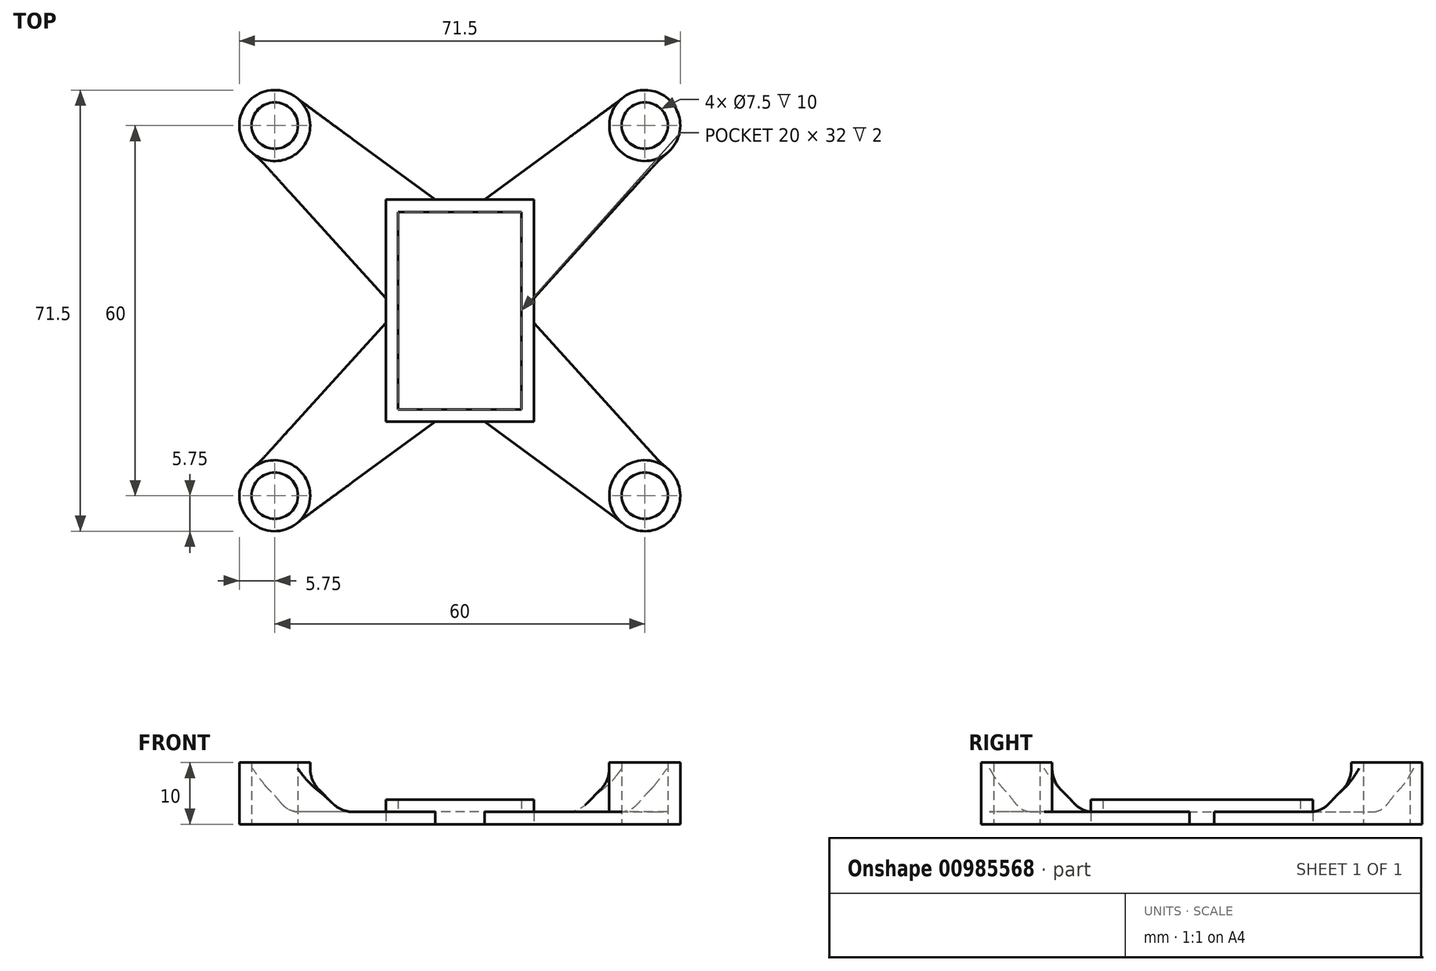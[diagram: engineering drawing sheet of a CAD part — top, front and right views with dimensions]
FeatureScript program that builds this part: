
annotation { "Feature Type Name" : "Feature", "Feature Type Description" : "" }
export const myFeature = defineFeature(function(context is Context, id is Id, definition is map)
    precondition{}
    {
        {
            var Q0;
            Q0=qCreatedBy(makeId("Top.planeOp"),FACE);
            var sketch = newSketch(context, id + "F0", { "sketchPlane" : qUnion([Q0])});
            skLineSegment(sketch, "E0.bottom", {"start": v(-30, 30) * mm, "end": v(30, 30) * mm, "construction": true});
            skLineSegment(sketch, "E0.top", {"start": v(-30, -30) * mm, "end": v(30, -30) * mm, "construction": true});
            skLineSegment(sketch, "E0.left", {"start": v(-30, 30) * mm, "end": v(-30, -30) * mm, "construction": true});
            skLineSegment(sketch, "E0.right", {"start": v(30, 30) * mm, "end": v(30, -30) * mm, "construction": true});
            skPoint(sketch, "E0.middle", {"position": v(0, 0) * mm});
            skCircle(sketch, "E1", {"center": v(-30, 30) * mm, "radius": 3.75 * mm});
            skCircle(sketch, "E2", {"center": v(30, 30) * mm, "radius": 3.75 * mm});
            skCircle(sketch, "E3", {"center": v(30, -30) * mm, "radius": 3.75 * mm});
            skCircle(sketch, "E4", {"center": v(-30, -30) * mm, "radius": 3.75 * mm});
            skCircle(sketch, "E5", {"center": v(-30, 30) * mm, "radius": 5.75 * mm});
            skCircle(sketch, "E6", {"center": v(30, 30) * mm, "radius": 5.75 * mm});
            skCircle(sketch, "E7", {"center": v(30, -30) * mm, "radius": 5.75 * mm});
            skCircle(sketch, "E8", {"center": v(-30, -30) * mm, "radius": 5.75 * mm});
            skLineSegment(sketch, "E9.bottom", {"start": v(-10, 16) * mm, "end": v(10, 16) * mm});
            skLineSegment(sketch, "E9.top", {"start": v(-10, -16) * mm, "end": v(10, -16) * mm});
            skLineSegment(sketch, "E9.left", {"start": v(-10, 16) * mm, "end": v(-10, -16) * mm});
            skLineSegment(sketch, "E9.right", {"start": v(10, 16) * mm, "end": v(10, -16) * mm});
            skLineSegment(sketch, "E10.bottom", {"start": v(-12, 18) * mm, "end": v(12, 18) * mm});
            skLineSegment(sketch, "E10.top", {"start": v(-12, -18) * mm, "end": v(12, -18) * mm});
            skLineSegment(sketch, "E10.left", {"start": v(-12, 18) * mm, "end": v(-12, -18) * mm});
            skLineSegment(sketch, "E10.right", {"start": v(12, 18) * mm, "end": v(12, -18) * mm});
            skLineSegment(sketch, "E11", {"start": v(-4, 18) * mm, "end": v(-26, 34.13) * mm});
            skLineSegment(sketch, "E12.MirrorCS", {"start": v(-12, 2) * mm, "end": v(-32.84, 25) * mm});
            skLineSegment(sketch, "E13.MirrorCS", {"start": v(4, 18) * mm, "end": v(26, 34.13) * mm});
            skLineSegment(sketch, "E14.MirrorCS", {"start": v(12, 2) * mm, "end": v(32.84, 25) * mm});
            skLineSegment(sketch, "E15.MirrorCS", {"start": v(-12, -2) * mm, "end": v(-32.84, -25) * mm});
            skLineSegment(sketch, "E16.MirrorCS", {"start": v(-4, -18) * mm, "end": v(-26, -34.13) * mm});
            skLineSegment(sketch, "E17.MirrorCS", {"start": v(4, -18) * mm, "end": v(26, -34.13) * mm});
            skLineSegment(sketch, "E18.MirrorCS", {"start": v(12, -2) * mm, "end": v(32.84, -25) * mm});
            skSolve(sketch);
        }
        {
            var Q0;
            {var subQ0=sQuery(id+"F0.wireOp",EDGE,"E11");Q0=makeQuery(id+"F0.imprint","IMPRINT",FACE,{"disambiguationData":[TD([[makeQuery(id+"F0.imprint","IMPRINT",EDGE,{"derivedFrom":subQ0}),1.0]])]});}
            var Q1;
            Q1=makeQuery(id+"F0.imprint","IMPRINT",FACE,{"disambiguationData":[TD([[makeQuery(id+"F0.imprint","IMPRINT",EDGE,{"derivedFrom":sQuery(id+"F0.wireOp",EDGE,"E1")}),-1.0]])]});
            var Q2;
            Q2=makeQuery(id+"F0.imprint","IMPRINT",FACE,{"disambiguationData":[TD([[makeQuery(id+"F0.imprint","IMPRINT",EDGE,{"derivedFrom":sQuery(id+"F0.wireOp",EDGE,"E2")}),-1.0]])]});
            var Q3;
            {var subQ0=sQuery(id+"F0.wireOp",EDGE,"E13.MirrorCS");Q3=makeQuery(id+"F0.imprint","IMPRINT",FACE,{"disambiguationData":[TD([[makeQuery(id+"F0.imprint","IMPRINT",EDGE,{"derivedFrom":subQ0}),-1.0]])]});}
            var Q4;
            Q4=makeQuery(id+"F0.imprint","IMPRINT",FACE,{"disambiguationData":[TD([[makeQuery(id+"F0.imprint","IMPRINT",EDGE,{"derivedFrom":sQuery(id+"F0.wireOp",EDGE,"E9.bottom")}),-1.0]])]});
            var Q5;
            Q5=makeQuery(id+"F0.imprint","IMPRINT",FACE,{"disambiguationData":[TD([[makeQuery(id+"F0.imprint","IMPRINT",EDGE,{"derivedFrom":sQuery(id+"F0.wireOp",EDGE,"E9.bottom")}),1.0]])]});
            var Q6;
            {var subQ0=sQuery(id+"F0.wireOp",EDGE,"E17.MirrorCS");Q6=makeQuery(id+"F0.imprint","IMPRINT",FACE,{"disambiguationData":[TD([[makeQuery(id+"F0.imprint","IMPRINT",EDGE,{"derivedFrom":subQ0}),1.0]])]});}
            var Q7;
            {var subQ0=sQuery(id+"F0.wireOp",EDGE,"E15.MirrorCS");Q7=makeQuery(id+"F0.imprint","IMPRINT",FACE,{"disambiguationData":[TD([[makeQuery(id+"F0.imprint","IMPRINT",EDGE,{"derivedFrom":subQ0}),1.0]])]});}
            var Q8;
            Q8=makeQuery(id+"F0.imprint","IMPRINT",FACE,{"disambiguationData":[TD([[makeQuery(id+"F0.imprint","IMPRINT",EDGE,{"derivedFrom":sQuery(id+"F0.wireOp",EDGE,"E4")}),-1.0]])]});
            var Q9;
            Q9=makeQuery(id+"F0.imprint","IMPRINT",FACE,{"disambiguationData":[TD([[makeQuery(id+"F0.imprint","IMPRINT",EDGE,{"derivedFrom":sQuery(id+"F0.wireOp",EDGE,"E3")}),-1.0]])]});
            extrude(context, id + "F1", {"entities" : qUnion([Q0, Q1, Q2, Q3, Q4, Q5, Q6, Q7, Q8, Q9]), "depth" : 2 * mm, "offsetDistance" : 25 * mm});
        }
        {
            var Q0;
            Q0=makeQuery(id+"F0.imprint","IMPRINT",FACE,{"disambiguationData":[TD([[makeQuery(id+"F0.imprint","IMPRINT",EDGE,{"derivedFrom":sQuery(id+"F0.wireOp",EDGE,"E4")}),-1.0]])]});
            var Q1;
            Q1=makeQuery(id+"F0.imprint","IMPRINT",FACE,{"disambiguationData":[TD([[makeQuery(id+"F0.imprint","IMPRINT",EDGE,{"derivedFrom":sQuery(id+"F0.wireOp",EDGE,"E3")}),-1.0]])]});
            var Q2;
            Q2=makeQuery(id+"F0.imprint","IMPRINT",FACE,{"disambiguationData":[TD([[makeQuery(id+"F0.imprint","IMPRINT",EDGE,{"derivedFrom":sQuery(id+"F0.wireOp",EDGE,"E1")}),-1.0]])]});
            var Q3;
            Q3=makeQuery(id+"F0.imprint","IMPRINT",FACE,{"disambiguationData":[TD([[makeQuery(id+"F0.imprint","IMPRINT",EDGE,{"derivedFrom":sQuery(id+"F0.wireOp",EDGE,"E2")}),-1.0]])]});
            var Q4;
            Q4=sQuery(id+"F0.wireOp",EDGE,"E5");
            var Q5;
            Q5=sQuery(id+"F0.wireOp",EDGE,"E1");
            var Q6;
            Q6=sQuery(id+"F0.wireOp",EDGE,"E2");
            var Q7;
            Q7=sQuery(id+"F0.wireOp",EDGE,"E6");
            var Q8;
            Q8=sQuery(id+"F0.wireOp",EDGE,"E3");
            var Q9;
            Q9=sQuery(id+"F0.wireOp",EDGE,"E7");
            var Q10;
            Q10=sQuery(id+"F0.wireOp",EDGE,"E4");
            var Q11;
            Q11=sQuery(id+"F0.wireOp",EDGE,"E8");
            extrude(context, id + "F2", {"entities" : qUnion([Q0, Q1, Q2, Q3]), "operationType" : NewBodyOperationType.ADD, "surfaceOperationType" : NewSurfaceOperationType.ADD, "surfaceEntities" : qUnion([Q4, Q5, Q6, Q7, Q8, Q9, Q10, Q11]), "depth" : 10 * mm, "offsetDistance" : 25 * mm});
        }
        {
            var Q0;
            Q0=makeQuery(id+"F0.imprint","IMPRINT",FACE,{"disambiguationData":[TD([[makeQuery(id+"F0.imprint","IMPRINT",EDGE,{"derivedFrom":sQuery(id+"F0.wireOp",EDGE,"E9.bottom")}),1.0]])]});
            extrude(context, id + "F3", {"entities" : qUnion([Q0]), "operationType" : NewBodyOperationType.ADD, "depth" : 4 * mm, "offsetDistance" : 25 * mm});
        }
        {
            var Q0;
            Q0=makeQuery(id+"F1.opExtrude","SWEPT_EDGE",EDGE,{"disambiguationData":[OSD([sQuery(id+"F0.wireOp",EDGE,"E8"),sQuery(id+"F0.wireOp",EDGE,"E15.MirrorCS")])]});
            var Q1;
            Q1=makeQuery(id+"F1.opExtrude","SWEPT_EDGE",EDGE,{"disambiguationData":[OSD([sQuery(id+"F0.wireOp",EDGE,"E5"),sQuery(id+"F0.wireOp",EDGE,"E11")])]});
            var Q2;
            Q2=makeQuery(id+"F1.opExtrude","SWEPT_EDGE",EDGE,{"disambiguationData":[OSD([sQuery(id+"F0.wireOp",EDGE,"E7"),sQuery(id+"F0.wireOp",EDGE,"E18.MirrorCS")])]});
            var Q3;
            Q3=makeQuery(id+"F1.opExtrude","SWEPT_EDGE",EDGE,{"disambiguationData":[OSD([sQuery(id+"F0.wireOp",EDGE,"E7"),sQuery(id+"F0.wireOp",EDGE,"E17.MirrorCS")])]});
            var Q4;
            Q4=makeQuery(id+"F1.opExtrude","SWEPT_EDGE",EDGE,{"disambiguationData":[OSD([sQuery(id+"F0.wireOp",EDGE,"E5"),sQuery(id+"F0.wireOp",EDGE,"E12.MirrorCS")])]});
            var Q5;
            Q5=makeQuery(id+"F1.opExtrude","SWEPT_EDGE",EDGE,{"disambiguationData":[OSD([sQuery(id+"F0.wireOp",EDGE,"E8"),sQuery(id+"F0.wireOp",EDGE,"E16.MirrorCS")])]});
            var Q6;
            Q6=makeQuery(id+"F1.opExtrude","SWEPT_EDGE",EDGE,{"disambiguationData":[OSD([sQuery(id+"F0.wireOp",EDGE,"E6"),sQuery(id+"F0.wireOp",EDGE,"E14.MirrorCS")])]});
            var Q7;
            Q7=makeQuery(id+"F1.opExtrude","SWEPT_EDGE",EDGE,{"disambiguationData":[OSD([sQuery(id+"F0.wireOp",EDGE,"E6"),sQuery(id+"F0.wireOp",EDGE,"E13.MirrorCS")])]});
            fillet(context, id + "F4", {"entities" : qUnion([Q0, Q1, Q2, Q3, Q4, Q5, Q6, Q7]), "radius" : 19 * mm, "tangentPropagation" : true, "allowEdgeOverflow" : false});
        }
        {
            var Q0;
            {var subQ0=sQuery(id+"F0.wireOp",EDGE,"E8");Q0=makeQuery(id+"F2.boolean.opBoolean","INTERSECT",EDGE,{"derivedFrom":[makeQuery(id+"F1.opExtrude","CAP_FACE",FACE,{"disambiguationData":[OSD([sQuery(id+"F0.wireOp",EDGE,"E1"),sQuery(id+"F0.wireOp",EDGE,"E2"),sQuery(id+"F0.wireOp",EDGE,"E3"),sQuery(id+"F0.wireOp",EDGE,"E4"),sQuery(id+"F0.wireOp",EDGE,"E5"),sQuery(id+"F0.wireOp",EDGE,"E6"),sQuery(id+"F0.wireOp",EDGE,"E7"),subQ0,sQuery(id+"F0.wireOp",EDGE,"E10.bottom"),sQuery(id+"F0.wireOp",EDGE,"E10.top"),sQuery(id+"F0.wireOp",EDGE,"E10.left"),sQuery(id+"F0.wireOp",EDGE,"E10.right"),sQuery(id+"F0.wireOp",EDGE,"E11"),sQuery(id+"F0.wireOp",EDGE,"E12.MirrorCS"),sQuery(id+"F0.wireOp",EDGE,"E13.MirrorCS"),sQuery(id+"F0.wireOp",EDGE,"E14.MirrorCS"),sQuery(id+"F0.wireOp",EDGE,"E15.MirrorCS"),sQuery(id+"F0.wireOp",EDGE,"E16.MirrorCS"),sQuery(id+"F0.wireOp",EDGE,"E17.MirrorCS"),sQuery(id+"F0.wireOp",EDGE,"E18.MirrorCS")])],"isStart":false}),makeQuery(id+"F2.opExtrude","SWEPT_FACE",FACE,{"disambiguationData":[OSD([subQ0])]})]});}
            var Q1;
            {var subQ0=sQuery(id+"F0.wireOp",EDGE,"E5");Q1=makeQuery(id+"F2.boolean.opBoolean","INTERSECT",EDGE,{"derivedFrom":[makeQuery(id+"F1.opExtrude","CAP_FACE",FACE,{"disambiguationData":[OSD([sQuery(id+"F0.wireOp",EDGE,"E1"),sQuery(id+"F0.wireOp",EDGE,"E2"),sQuery(id+"F0.wireOp",EDGE,"E3"),sQuery(id+"F0.wireOp",EDGE,"E4"),subQ0,sQuery(id+"F0.wireOp",EDGE,"E6"),sQuery(id+"F0.wireOp",EDGE,"E7"),sQuery(id+"F0.wireOp",EDGE,"E8"),sQuery(id+"F0.wireOp",EDGE,"E10.bottom"),sQuery(id+"F0.wireOp",EDGE,"E10.top"),sQuery(id+"F0.wireOp",EDGE,"E10.left"),sQuery(id+"F0.wireOp",EDGE,"E10.right"),sQuery(id+"F0.wireOp",EDGE,"E11"),sQuery(id+"F0.wireOp",EDGE,"E12.MirrorCS"),sQuery(id+"F0.wireOp",EDGE,"E13.MirrorCS"),sQuery(id+"F0.wireOp",EDGE,"E14.MirrorCS"),sQuery(id+"F0.wireOp",EDGE,"E15.MirrorCS"),sQuery(id+"F0.wireOp",EDGE,"E16.MirrorCS"),sQuery(id+"F0.wireOp",EDGE,"E17.MirrorCS"),sQuery(id+"F0.wireOp",EDGE,"E18.MirrorCS")])],"isStart":false}),makeQuery(id+"F2.opExtrude","SWEPT_FACE",FACE,{"disambiguationData":[OSD([subQ0])]})]});}
            var Q2;
            {var subQ0=sQuery(id+"F0.wireOp",EDGE,"E6");Q2=makeQuery(id+"F2.boolean.opBoolean","INTERSECT",EDGE,{"derivedFrom":[makeQuery(id+"F1.opExtrude","CAP_FACE",FACE,{"disambiguationData":[OSD([sQuery(id+"F0.wireOp",EDGE,"E1"),sQuery(id+"F0.wireOp",EDGE,"E2"),sQuery(id+"F0.wireOp",EDGE,"E3"),sQuery(id+"F0.wireOp",EDGE,"E4"),sQuery(id+"F0.wireOp",EDGE,"E5"),subQ0,sQuery(id+"F0.wireOp",EDGE,"E7"),sQuery(id+"F0.wireOp",EDGE,"E8"),sQuery(id+"F0.wireOp",EDGE,"E10.bottom"),sQuery(id+"F0.wireOp",EDGE,"E10.top"),sQuery(id+"F0.wireOp",EDGE,"E10.left"),sQuery(id+"F0.wireOp",EDGE,"E10.right"),sQuery(id+"F0.wireOp",EDGE,"E11"),sQuery(id+"F0.wireOp",EDGE,"E12.MirrorCS"),sQuery(id+"F0.wireOp",EDGE,"E13.MirrorCS"),sQuery(id+"F0.wireOp",EDGE,"E14.MirrorCS"),sQuery(id+"F0.wireOp",EDGE,"E15.MirrorCS"),sQuery(id+"F0.wireOp",EDGE,"E16.MirrorCS"),sQuery(id+"F0.wireOp",EDGE,"E17.MirrorCS"),sQuery(id+"F0.wireOp",EDGE,"E18.MirrorCS")])],"isStart":false}),makeQuery(id+"F2.opExtrude","SWEPT_FACE",FACE,{"disambiguationData":[OSD([subQ0])]})]});}
            chamfer(context, id + "F5", {"entities" : qUnion([Q0, Q1, Q2]), "width" : 5 * mm, "tangentPropagation" : true});
        }
        {
            var Q0;
            {var subQ0=sQuery(id+"F0.wireOp",EDGE,"E8");var subQ1=makeQuery(id+"F2.opExtrude","SWEPT_FACE",FACE,{"disambiguationData":[OSD([subQ0])]});Q0=makeQuery(id+"F5.opChamfer","BLEND_EDGE",EDGE,{"blendedFrom":[makeQuery(id+"F2.boolean.opBoolean","INTERSECT",EDGE,{"derivedFrom":[makeQuery(id+"F1.opExtrude","CAP_FACE",FACE,{"disambiguationData":[OSD([sQuery(id+"F0.wireOp",EDGE,"E1"),sQuery(id+"F0.wireOp",EDGE,"E2"),sQuery(id+"F0.wireOp",EDGE,"E3"),sQuery(id+"F0.wireOp",EDGE,"E4"),sQuery(id+"F0.wireOp",EDGE,"E5"),sQuery(id+"F0.wireOp",EDGE,"E6"),sQuery(id+"F0.wireOp",EDGE,"E7"),subQ0,sQuery(id+"F0.wireOp",EDGE,"E10.bottom"),sQuery(id+"F0.wireOp",EDGE,"E10.top"),sQuery(id+"F0.wireOp",EDGE,"E10.left"),sQuery(id+"F0.wireOp",EDGE,"E10.right"),sQuery(id+"F0.wireOp",EDGE,"E11"),sQuery(id+"F0.wireOp",EDGE,"E12.MirrorCS"),sQuery(id+"F0.wireOp",EDGE,"E13.MirrorCS"),sQuery(id+"F0.wireOp",EDGE,"E14.MirrorCS"),sQuery(id+"F0.wireOp",EDGE,"E15.MirrorCS"),sQuery(id+"F0.wireOp",EDGE,"E16.MirrorCS"),sQuery(id+"F0.wireOp",EDGE,"E17.MirrorCS"),sQuery(id+"F0.wireOp",EDGE,"E18.MirrorCS")])],"isStart":false}),subQ1]}),makeQuery(id+"F2.boolean.opBoolean","MERGE",FACE,{"derivedFrom":[makeQuery(id+"F1.opExtrude","SWEPT_FACE",FACE,{"disambiguationData":[OSD([subQ0])]}),subQ1]})],"blendedInto":[makeQuery(id+"F2.boolean.opBoolean","MERGE",FACE,{"derivedFrom":[makeQuery(id+"F1.opExtrude","SWEPT_FACE",FACE,{"disambiguationData":[OSD([subQ0])]}),subQ1]})]});}
            var Q1;
            {var subQ0=sQuery(id+"F0.wireOp",EDGE,"E15.MirrorCS");var subQ1=sQuery(id+"F0.wireOp",EDGE,"E10.left");var subQ2=sQuery(id+"F0.wireOp",EDGE,"E10.top");var subQ3=sQuery(id+"F0.wireOp",EDGE,"E8");var subQ4=sQuery(id+"F0.wireOp",EDGE,"E16.MirrorCS");var subQ5=makeQuery(id+"F2.opExtrude","SWEPT_FACE",FACE,{"disambiguationData":[OSD([subQ3])]});var subQ6=makeQuery(id+"F1.opExtrude","CAP_FACE",FACE,{"disambiguationData":[OSD([sQuery(id+"F0.wireOp",EDGE,"E1"),sQuery(id+"F0.wireOp",EDGE,"E2"),sQuery(id+"F0.wireOp",EDGE,"E3"),sQuery(id+"F0.wireOp",EDGE,"E4"),sQuery(id+"F0.wireOp",EDGE,"E5"),sQuery(id+"F0.wireOp",EDGE,"E6"),sQuery(id+"F0.wireOp",EDGE,"E7"),subQ3,sQuery(id+"F0.wireOp",EDGE,"E10.bottom"),subQ2,subQ1,sQuery(id+"F0.wireOp",EDGE,"E10.right"),sQuery(id+"F0.wireOp",EDGE,"E11"),sQuery(id+"F0.wireOp",EDGE,"E12.MirrorCS"),sQuery(id+"F0.wireOp",EDGE,"E13.MirrorCS"),sQuery(id+"F0.wireOp",EDGE,"E14.MirrorCS"),subQ0,subQ4,sQuery(id+"F0.wireOp",EDGE,"E17.MirrorCS"),sQuery(id+"F0.wireOp",EDGE,"E18.MirrorCS")])],"isStart":false});Q1=makeQuery(id+"F5.opChamfer","BLEND_EDGE",EDGE,{"blendedFrom":[makeQuery(id+"F2.boolean.opBoolean","INTERSECT",EDGE,{"derivedFrom":[subQ6,subQ5]}),makeQuery(id+"F3.boolean.opBoolean","SPLIT",FACE,{"disambiguationData":[TD([makeQuery(id+"F1.opExtrude","SWEPT_FACE",FACE,{"disambiguationData":[OSD([subQ3])]})])],"derivedFrom":subQ6})],"blendedInto":[makeQuery(id+"F3.boolean.opBoolean","SPLIT",FACE,{"disambiguationData":[TD([makeQuery(id+"F1.opExtrude","SWEPT_FACE",FACE,{"disambiguationData":[OSD([subQ3])]})])],"derivedFrom":subQ6})]});}
            var Q2;
            {var subQ0=sQuery(id+"F0.wireOp",EDGE,"E5");var subQ1=makeQuery(id+"F2.opExtrude","SWEPT_FACE",FACE,{"disambiguationData":[OSD([subQ0])]});Q2=makeQuery(id+"F5.opChamfer","BLEND_EDGE",EDGE,{"blendedFrom":[makeQuery(id+"F2.boolean.opBoolean","INTERSECT",EDGE,{"derivedFrom":[makeQuery(id+"F1.opExtrude","CAP_FACE",FACE,{"disambiguationData":[OSD([sQuery(id+"F0.wireOp",EDGE,"E1"),sQuery(id+"F0.wireOp",EDGE,"E2"),sQuery(id+"F0.wireOp",EDGE,"E3"),sQuery(id+"F0.wireOp",EDGE,"E4"),subQ0,sQuery(id+"F0.wireOp",EDGE,"E6"),sQuery(id+"F0.wireOp",EDGE,"E7"),sQuery(id+"F0.wireOp",EDGE,"E8"),sQuery(id+"F0.wireOp",EDGE,"E10.bottom"),sQuery(id+"F0.wireOp",EDGE,"E10.top"),sQuery(id+"F0.wireOp",EDGE,"E10.left"),sQuery(id+"F0.wireOp",EDGE,"E10.right"),sQuery(id+"F0.wireOp",EDGE,"E11"),sQuery(id+"F0.wireOp",EDGE,"E12.MirrorCS"),sQuery(id+"F0.wireOp",EDGE,"E13.MirrorCS"),sQuery(id+"F0.wireOp",EDGE,"E14.MirrorCS"),sQuery(id+"F0.wireOp",EDGE,"E15.MirrorCS"),sQuery(id+"F0.wireOp",EDGE,"E16.MirrorCS"),sQuery(id+"F0.wireOp",EDGE,"E17.MirrorCS"),sQuery(id+"F0.wireOp",EDGE,"E18.MirrorCS")])],"isStart":false}),subQ1]}),makeQuery(id+"F2.boolean.opBoolean","MERGE",FACE,{"derivedFrom":[makeQuery(id+"F1.opExtrude","SWEPT_FACE",FACE,{"disambiguationData":[OSD([subQ0])]}),subQ1]})],"blendedInto":[makeQuery(id+"F2.boolean.opBoolean","MERGE",FACE,{"derivedFrom":[makeQuery(id+"F1.opExtrude","SWEPT_FACE",FACE,{"disambiguationData":[OSD([subQ0])]}),subQ1]})]});}
            var Q3;
            {var subQ0=sQuery(id+"F0.wireOp",EDGE,"E11");var subQ1=sQuery(id+"F0.wireOp",EDGE,"E10.left");var subQ2=sQuery(id+"F0.wireOp",EDGE,"E10.bottom");var subQ3=sQuery(id+"F0.wireOp",EDGE,"E5");var subQ4=sQuery(id+"F0.wireOp",EDGE,"E12.MirrorCS");var subQ5=makeQuery(id+"F2.opExtrude","SWEPT_FACE",FACE,{"disambiguationData":[OSD([subQ3])]});var subQ6=makeQuery(id+"F1.opExtrude","CAP_FACE",FACE,{"disambiguationData":[OSD([sQuery(id+"F0.wireOp",EDGE,"E1"),sQuery(id+"F0.wireOp",EDGE,"E2"),sQuery(id+"F0.wireOp",EDGE,"E3"),sQuery(id+"F0.wireOp",EDGE,"E4"),subQ3,sQuery(id+"F0.wireOp",EDGE,"E6"),sQuery(id+"F0.wireOp",EDGE,"E7"),sQuery(id+"F0.wireOp",EDGE,"E8"),subQ2,sQuery(id+"F0.wireOp",EDGE,"E10.top"),subQ1,sQuery(id+"F0.wireOp",EDGE,"E10.right"),subQ0,subQ4,sQuery(id+"F0.wireOp",EDGE,"E13.MirrorCS"),sQuery(id+"F0.wireOp",EDGE,"E14.MirrorCS"),sQuery(id+"F0.wireOp",EDGE,"E15.MirrorCS"),sQuery(id+"F0.wireOp",EDGE,"E16.MirrorCS"),sQuery(id+"F0.wireOp",EDGE,"E17.MirrorCS"),sQuery(id+"F0.wireOp",EDGE,"E18.MirrorCS")])],"isStart":false});Q3=makeQuery(id+"F5.opChamfer","BLEND_EDGE",EDGE,{"blendedFrom":[makeQuery(id+"F2.boolean.opBoolean","INTERSECT",EDGE,{"derivedFrom":[subQ6,subQ5]}),makeQuery(id+"F3.boolean.opBoolean","SPLIT",FACE,{"disambiguationData":[TD([makeQuery(id+"F1.opExtrude","SWEPT_FACE",FACE,{"disambiguationData":[OSD([subQ3])]})])],"derivedFrom":subQ6})],"blendedInto":[makeQuery(id+"F3.boolean.opBoolean","SPLIT",FACE,{"disambiguationData":[TD([makeQuery(id+"F1.opExtrude","SWEPT_FACE",FACE,{"disambiguationData":[OSD([subQ3])]})])],"derivedFrom":subQ6})]});}
            var Q4;
            {var subQ0=sQuery(id+"F0.wireOp",EDGE,"E13.MirrorCS");var subQ1=sQuery(id+"F0.wireOp",EDGE,"E10.right");var subQ2=sQuery(id+"F0.wireOp",EDGE,"E10.bottom");var subQ3=sQuery(id+"F0.wireOp",EDGE,"E6");var subQ4=sQuery(id+"F0.wireOp",EDGE,"E14.MirrorCS");var subQ5=makeQuery(id+"F2.opExtrude","SWEPT_FACE",FACE,{"disambiguationData":[OSD([subQ3])]});var subQ6=makeQuery(id+"F1.opExtrude","CAP_FACE",FACE,{"disambiguationData":[OSD([sQuery(id+"F0.wireOp",EDGE,"E1"),sQuery(id+"F0.wireOp",EDGE,"E2"),sQuery(id+"F0.wireOp",EDGE,"E3"),sQuery(id+"F0.wireOp",EDGE,"E4"),sQuery(id+"F0.wireOp",EDGE,"E5"),subQ3,sQuery(id+"F0.wireOp",EDGE,"E7"),sQuery(id+"F0.wireOp",EDGE,"E8"),subQ2,sQuery(id+"F0.wireOp",EDGE,"E10.top"),sQuery(id+"F0.wireOp",EDGE,"E10.left"),subQ1,sQuery(id+"F0.wireOp",EDGE,"E11"),sQuery(id+"F0.wireOp",EDGE,"E12.MirrorCS"),subQ0,subQ4,sQuery(id+"F0.wireOp",EDGE,"E15.MirrorCS"),sQuery(id+"F0.wireOp",EDGE,"E16.MirrorCS"),sQuery(id+"F0.wireOp",EDGE,"E17.MirrorCS"),sQuery(id+"F0.wireOp",EDGE,"E18.MirrorCS")])],"isStart":false});Q4=makeQuery(id+"F5.opChamfer","BLEND_EDGE",EDGE,{"blendedFrom":[makeQuery(id+"F2.boolean.opBoolean","INTERSECT",EDGE,{"derivedFrom":[subQ6,subQ5]}),makeQuery(id+"F3.boolean.opBoolean","SPLIT",FACE,{"disambiguationData":[TD([makeQuery(id+"F1.opExtrude","SWEPT_FACE",FACE,{"disambiguationData":[OSD([subQ3])]})])],"derivedFrom":subQ6})],"blendedInto":[makeQuery(id+"F3.boolean.opBoolean","SPLIT",FACE,{"disambiguationData":[TD([makeQuery(id+"F1.opExtrude","SWEPT_FACE",FACE,{"disambiguationData":[OSD([subQ3])]})])],"derivedFrom":subQ6})]});}
            var Q5;
            {var subQ0=sQuery(id+"F0.wireOp",EDGE,"E6");var subQ1=makeQuery(id+"F2.opExtrude","SWEPT_FACE",FACE,{"disambiguationData":[OSD([subQ0])]});Q5=makeQuery(id+"F5.opChamfer","BLEND_EDGE",EDGE,{"blendedFrom":[makeQuery(id+"F2.boolean.opBoolean","INTERSECT",EDGE,{"derivedFrom":[makeQuery(id+"F1.opExtrude","CAP_FACE",FACE,{"disambiguationData":[OSD([sQuery(id+"F0.wireOp",EDGE,"E1"),sQuery(id+"F0.wireOp",EDGE,"E2"),sQuery(id+"F0.wireOp",EDGE,"E3"),sQuery(id+"F0.wireOp",EDGE,"E4"),sQuery(id+"F0.wireOp",EDGE,"E5"),subQ0,sQuery(id+"F0.wireOp",EDGE,"E7"),sQuery(id+"F0.wireOp",EDGE,"E8"),sQuery(id+"F0.wireOp",EDGE,"E10.bottom"),sQuery(id+"F0.wireOp",EDGE,"E10.top"),sQuery(id+"F0.wireOp",EDGE,"E10.left"),sQuery(id+"F0.wireOp",EDGE,"E10.right"),sQuery(id+"F0.wireOp",EDGE,"E11"),sQuery(id+"F0.wireOp",EDGE,"E12.MirrorCS"),sQuery(id+"F0.wireOp",EDGE,"E13.MirrorCS"),sQuery(id+"F0.wireOp",EDGE,"E14.MirrorCS"),sQuery(id+"F0.wireOp",EDGE,"E15.MirrorCS"),sQuery(id+"F0.wireOp",EDGE,"E16.MirrorCS"),sQuery(id+"F0.wireOp",EDGE,"E17.MirrorCS"),sQuery(id+"F0.wireOp",EDGE,"E18.MirrorCS")])],"isStart":false}),subQ1]}),makeQuery(id+"F2.boolean.opBoolean","MERGE",FACE,{"derivedFrom":[makeQuery(id+"F1.opExtrude","SWEPT_FACE",FACE,{"disambiguationData":[OSD([subQ0])]}),subQ1]})],"blendedInto":[makeQuery(id+"F2.boolean.opBoolean","MERGE",FACE,{"derivedFrom":[makeQuery(id+"F1.opExtrude","SWEPT_FACE",FACE,{"disambiguationData":[OSD([subQ0])]}),subQ1]})]});}
            fillet(context, id + "F6", {"entities" : qUnion([Q0, Q1, Q2, Q3, Q4, Q5]), "radius" : 5 * mm, "tangentPropagation" : true, "allowEdgeOverflow" : false});
        }
    });
